# Revit family: REC-PARA2001208R
name_source: partatom
category: Structural Connections
units: mm (PartAtom-declared; Revit-internal decimal feet)

## family parameters
Cut with Voids When Loaded = Yes
Enable Cutting in Views = Yes
Host = Face
Material for Model Behavior = Steel
Shared = No

## types (1)
- PARA2001208R
    Classification.Uniclass.Pr.Description = Brackets
    Classification.Uniclass.Pr.Number = Pr_20_85_09
    Cost = 0 $
    Creado por: = Deliprogal SL
    Default Elevation = 0 mm  [stored 0 ft]
    Description = Non-slip reinforced angle plate 200x120x80x8 mm with the slotted hole 64X17 mm on one side and 2 holes Ø17 mm on another side.
    Description_ESP = Pletina angular reforzada antideslizante 200x120x80x8 mm, coliso 17x 64 mm en una ala y 2TØ17 mm en la otra.
    Export Type to IFC As = IfcElementAssembly
    Fecha Ultima Revision: = 01/03/2024
    Fecha de Creacion: = 01/03/2024
    IFCExportAs = IfcElementAssembly
    IFCExportType = Brackets
    Keynote = Anti-tilt anchor for fixing panels to concrete structures or as a bracket for supporting panels on horizontal slabs by means of the interposition of profiles and/or expansion anchor bolts.
    Keynote_ESP = Anclaje antivuelco para fijación de paneles a estructura de hormigón o como ménsula para la sustentación de paneles sobre forjados horizontales mediante la interposición de perfiles y/ó tornillos de anclaje expansivo.
    Manufacturer = RECENSE
    Model = PARA2001208R
    Type IFC Predefined Type = Brackets
    URL = https://recense.com
    Visible = Yes

note: [stored X ft] marks values corroborated as IEEE doubles in the binary element streams (Revit-internal decimal feet)

## geometry (parser evidence)
native form markers: Sweep x3
no freeform markers — native parametric forms only
